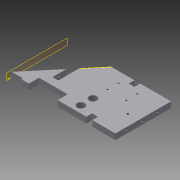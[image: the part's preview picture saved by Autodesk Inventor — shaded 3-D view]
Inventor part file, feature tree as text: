
AUTODESK INVENTOR PART (.ipt)
format: ipt  version: 2012 (Build 160160000, 160)  size: 239,104 bytes
history: native  units: mm
features: sketch x19, reference x18, hole x11, extrude x7, plane x1, projected_geometry x1
ambient origin geometry x8: Origin, YZ Plane, XZ Plane, XY Plane, X Axis, Y Axis, Z Axis, Center Point
bodies: Solid1 (feature_tree)
feature tree (57):
  extrude  "Extrusion1"  Depth=91.44mm
  extrude  "Extrusion2"  Depth=8.726646mm
  extrude  "Extrusion3"  Depth=12.7mm
  extrude  "Extrusion4"  Depth=33.02mm
  extrude  "Extrusion5"  Depth=16.51mm TaperAngle=0.0deg
  extrude  "Extrusion6"  Depth=9.525mm
  extrude  "Extrusion7"  Depth=20.32mm
  hole  "Hole7"  [1 undecoded]
  hole  "Hole8"  [1 undecoded]
  hole  "Hole9"  [1 undecoded]
  hole  "Hole10"  [1 undecoded]
  hole  "Hole11"  [1 undecoded]
  hole  "Hole12"  [1 undecoded]
  hole  "Hole13"  [1 undecoded]
  hole  "Hole14"  [1 undecoded]
  hole  "Hole15"  [1 undecoded]
  plane  "Work Plane1"
  hole  "Hole16"  [1 undecoded]
  hole  "Hole17"  [1 undecoded]
  sketch  "Sketch27"  dims[d169=3.302mm d170=12.7mm d171=9.525mm d172=6.35mm d173=14.3117mm d174=7.62mm d175=20.594885mm d176=1.7018mm d177=12.7mm d178=9.525mm d179=6.35mm d180=14.3117mm d181=2.54mm d182=20.594885mm d183=1.7018mm d184=12.7mm d185=9.525mm d186=6.35mm d187=14.3117mm d188=5.08mm d189=20.594885mm d190=-175.0mm d191=3.302mm d192=12.7mm d193=8.4328mm d194=6.35mm d195=14.3117mm d196=76.2mm d197=20.594885mm d198=2.6416mm d199=4.964769mm d200=3.302mm d201=12.7mm d202=8.4328mm d203=6.35mm d204=14.3117mm d205=4.7625mm d206=20.594885mm d63=1.0mm d64=1.0mm]
  sketch  "Sketch1"  dims[d0=175.0mm d1=91.44mm]
  sketch  "Sketch8"  dims[d3=9.525mm d4=0.0mm d100=8.726646mm]
  reference  "Reference3"
  reference  "Reference4"
  sketch  "Sketch9"  dims[d101=12.7mm d102=12.7mm]
  sketch  "Sketch12"  dims[d103=25.4mm d104=0.0mm d105=33.02mm]
  projected_geometry  "Projected Loop2"
  sketch  "Sketch13"  dims[d106=46.99mm d107=16.51mm d108=0.0mm]
  sketch  "Sketch14"  dims[d109=24.13mm d110=9.525mm]
  sketch  "Sketch15"  dims[d111=62.992mm d112=0.0mm d113=20.32mm]
  sketch  "Sketch16"  dims[d114=2.54mm d115=0.0mm d116=9.525mm]
  reference  "Reference7"
  sketch  "Sketch17"  dims[d117=38.1mm d118=9.525mm d119=0.0mm]
  reference  "Reference8"
  sketch  "Sketch18"  dims[d120=38.1mm d121=9.525mm]
  reference  "Reference9"
  reference  "Reference10"
  sketch  "Sketch19"  dims[d122=9.525mm d123=0.0mm]
  reference  "Reference11"
  reference  "Reference12"
  reference  "Reference13"
  reference  "Reference14"
  sketch  "Sketch20"  dims[d124=3.302mm d125=12.7mm d126=9.525mm d127=6.35mm d128=14.3117mm d129=10.16mm d130=20.594885mm]
  sketch  "Sketch21"  dims[d131=3.302mm d132=12.7mm d133=9.525mm d134=6.35mm d135=14.3117mm d136=12.7mm d137=20.594885mm]
  reference  "Reference15"
  reference  "Reference16"
  reference  "Reference17"
  sketch  "Sketch22"  dims[d138=3.302mm d139=12.7mm d140=9.525mm d141=6.35mm d142=14.3117mm d143=10.16mm d144=20.594885mm]
  reference  "Reference18"
  sketch  "Sketch23"  dims[d145=2.6416mm d146=12.7mm d147=9.525mm d148=6.35mm d149=14.3117mm d150=10.16mm d151=20.594885mm d152=19.304mm]
  reference  "Reference19"
  sketch  "Sketch24"  dims[d153=44.45mm d154=69.85mm]
  reference  "Reference20"
  sketch  "Sketch25"  dims[d155=3.302mm d156=12.7mm d157=9.525mm d158=6.35mm d159=14.3117mm d160=12.7mm d161=20.594885mm]
  reference  "Reference21"
  sketch  "Sketch26"  dims[d162=3.302mm d163=12.7mm d164=9.525mm d165=6.35mm d166=14.3117mm d167=7.62mm d168=20.594885mm]
  reference  "Reference22"
note: 11 required parameter values undecoded (feature->parameter linkage not recoverable at this tier; creation-order binding heuristic only, values carry confidence <= 0.55)
